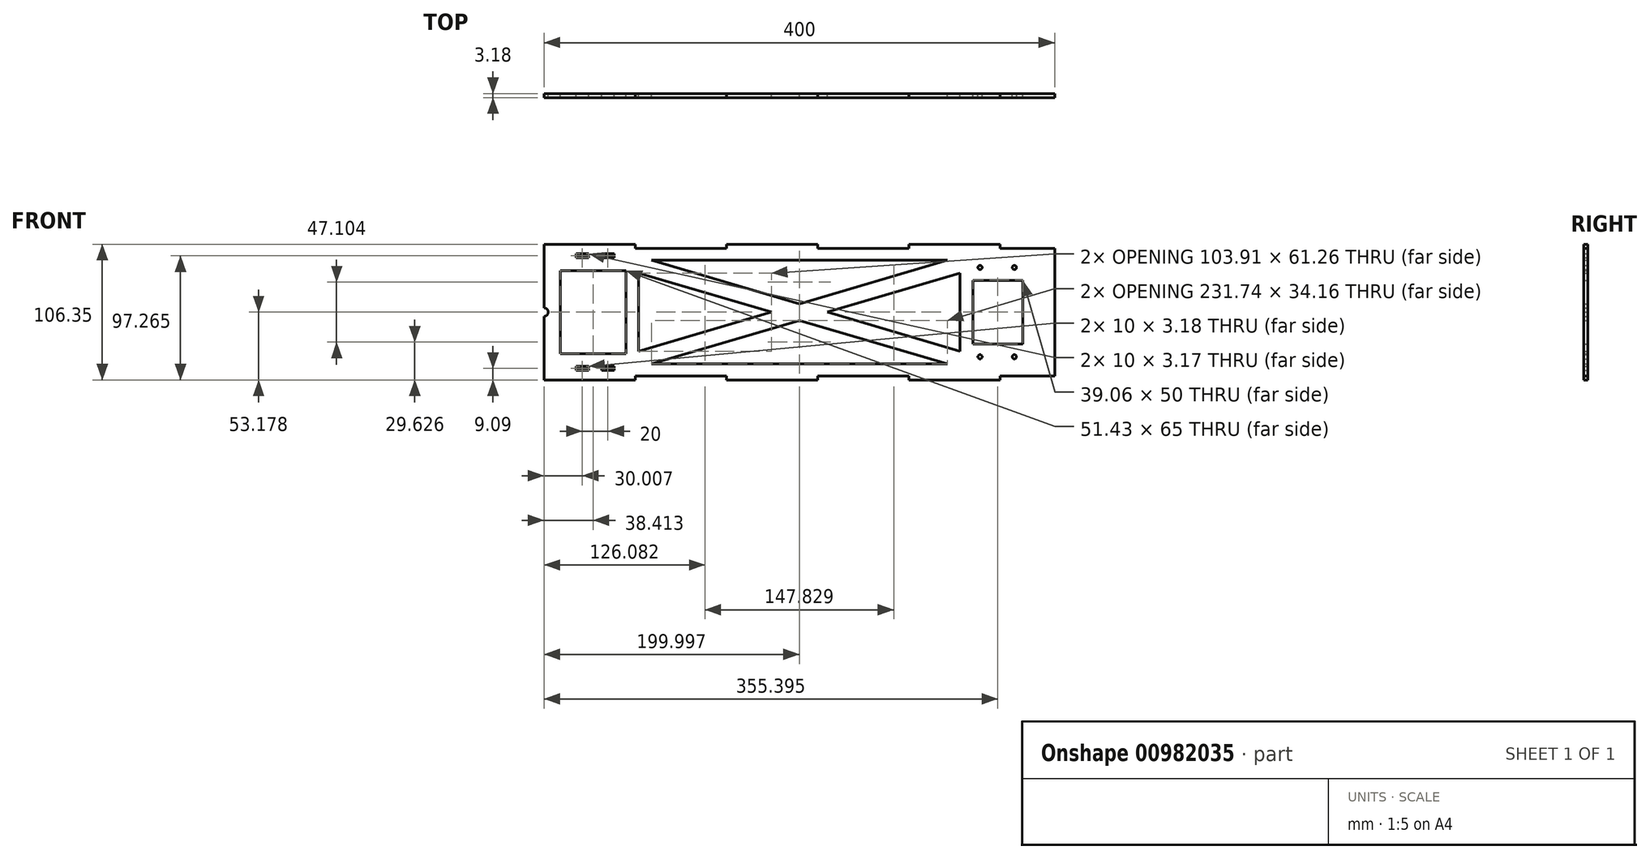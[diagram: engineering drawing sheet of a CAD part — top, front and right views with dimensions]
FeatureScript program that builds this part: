
annotation { "Feature Type Name" : "Feature", "Feature Type Description" : "" }
export const myFeature = defineFeature(function(context is Context, id is Id, definition is map)
    precondition{}
    {
        {
            var Q0;
            Q0=qCreatedBy(makeId("Front.planeOp"),FACE);
            var sketch = newSketch(context, id + "F0", { "sketchPlane" : qUnion([Q0])});
            skLineSegment(sketch, "E0.bottom", {"start": v(122.16, -35.2) * mm, "end": v(-277.84, -35.2) * mm, "construction": true});
            skLineSegment(sketch, "E0.top", {"start": v(122.16, 64.8) * mm, "end": v(-277.84, 64.8) * mm, "construction": true});
            skLineSegment(sketch, "E0.left", {"start": v(122.16, -35.2) * mm, "end": v(122.16, 64.8) * mm});
            skLineSegment(sketch, "E0.right", {"start": v(-277.84, -35.2) * mm, "end": v(-277.84, 64.8) * mm});
            skLineSegment(sketch, "E1", {"start": v(-237.84, 42.25) * mm, "end": v(-233.84, 42.25) * mm, "construction": true});
            skLineSegment(sketch, "E2", {"start": v(-237.84, 42.25) * mm, "end": v(-237.84, 46.25) * mm, "construction": true});
            skLineSegment(sketch, "E3", {"start": v(-237.84, -12.65) * mm, "end": v(-233.84, -12.65) * mm, "construction": true});
            skLineSegment(sketch, "E4", {"start": v(-237.84, -12.65) * mm, "end": v(-237.84, -8.65) * mm, "construction": true});
            skCircle(sketch, "E5", {"center": v(77.16, -20.2) * mm, "radius": 4 * mm, "construction": true});
            skLineSegment(sketch, "E6", {"start": v(77.16, -20.2) * mm, "end": v(81.16, -20.2) * mm, "construction": true});
            skLineSegment(sketch, "E7", {"start": v(77.16, -20.2) * mm, "end": v(77.16, -16.2) * mm, "construction": true});
            skCircle(sketch, "E8", {"center": v(90.63, -20.2) * mm, "radius": 1.64 * mm});
            skCircle(sketch, "E9.MirrorC", {"center": v(63.68, -20.2) * mm, "radius": 1.64 * mm});
            skCircle(sketch, "E10", {"center": v(77.16, 49.8) * mm, "radius": 4 * mm, "construction": true});
            skLineSegment(sketch, "E11", {"start": v(77.16, 49.8) * mm, "end": v(81.16, 49.8) * mm, "construction": true});
            skLineSegment(sketch, "E12", {"start": v(77.16, 49.8) * mm, "end": v(77.16, 53.8) * mm, "construction": true});
            skCircle(sketch, "E13", {"center": v(90.63, 49.8) * mm, "radius": 1.64 * mm});
            skCircle(sketch, "E14.MirrorC", {"center": v(63.68, 49.8) * mm, "radius": 1.64 * mm});
            skPoint(sketch, "E15.middle.positionSnap0", {"position": v(-237.84, -10.65) * mm});
            skPoint(sketch, "E15.centerSnap0", {"position": v(-237.84, -10.65) * mm});
            skLineSegment(sketch, "E16", {"start": v(-77.84, 64.8) * mm, "end": v(-77.84, -35.2) * mm, "construction": true});
            skLineSegment(sketch, "E17", {"start": v(-77.84, 14.8) * mm, "end": v(-277.84, 14.8) * mm, "construction": true});
            skLineSegment(sketch, "E18.right", {"start": v(-265.14, -17.7) * mm, "end": v(-265.14, 47.3) * mm});
            skLineSegment(sketch, "E19", {"start": v(-77.84, 14.8) * mm, "end": v(122.16, 14.8) * mm, "construction": true});
            skLineSegment(sketch, "E20.right", {"start": v(97.09, 39.8) * mm, "end": v(97.09, -10.2) * mm});
            skLineSegment(sketch, "E21.right", {"start": v(-213.71, 47.3) * mm, "end": v(-213.71, -17.7) * mm});
            skLineSegment(sketch, "E22", {"start": v(-265.14, 47.3) * mm, "end": v(-213.71, 47.3) * mm});
            skLineSegment(sketch, "E23", {"start": v(-265.14, -17.7) * mm, "end": v(-213.71, -17.7) * mm});
            skLineSegment(sketch, "E24.right", {"start": v(58.02, 39.8) * mm, "end": v(58.02, -10.2) * mm});
            skLineSegment(sketch, "E25", {"start": v(58.02, 39.8) * mm, "end": v(97.09, 39.8) * mm});
            skLineSegment(sketch, "E26", {"start": v(58.02, -10.2) * mm, "end": v(97.09, -10.2) * mm});
            skLineSegment(sketch, "E27.top", {"start": v(-277.84, -38.38) * mm, "end": v(-206.41, -38.38) * mm});
            skLineSegment(sketch, "E27.left", {"start": v(-277.84, -35.2) * mm, "end": v(-277.84, -38.38) * mm});
            skLineSegment(sketch, "E27.right", {"start": v(-206.41, -35.2) * mm, "end": v(-206.41, -38.38) * mm});
            skLineSegment(sketch, "E28.bottom", {"start": v(-206.41, -35.2) * mm, "end": v(-134.99, -35.2) * mm});
            skLineSegment(sketch, "E29.1.0.0", {"start": v(-134.99, -38.38) * mm, "end": v(-63.56, -38.38) * mm});
            skLineSegment(sketch, "E29.1.0.1", {"start": v(-63.56, -35.2) * mm, "end": v(7.87, -35.2) * mm});
            skLineSegment(sketch, "E29.1.0.2", {"start": v(-134.99, -35.2) * mm, "end": v(-134.99, -38.38) * mm});
            skLineSegment(sketch, "E29.1.0.3", {"start": v(-63.56, -35.2) * mm, "end": v(-63.56, -38.38) * mm});
            skLineSegment(sketch, "E29.1.0.4", {"start": v(-63.56, -35.2) * mm, "end": v(-63.56, -38.38) * mm});
            skLineSegment(sketch, "E29.2.0.0", {"start": v(7.87, -38.38) * mm, "end": v(79.3, -38.38) * mm});
            skLineSegment(sketch, "E29.2.0.2", {"start": v(7.87, -35.2) * mm, "end": v(7.87, -38.38) * mm});
            skLineSegment(sketch, "E29.direction1", {"start": v(-277.84, -38.38) * mm, "end": v(-134.99, -38.38) * mm, "construction": true});
            skLineSegment(sketch, "E30.MirrorCS", {"start": v(-63.56, 64.8) * mm, "end": v(-63.56, 67.97) * mm});
            skLineSegment(sketch, "E31.MirrorCS", {"start": v(-206.41, 64.8) * mm, "end": v(-206.41, 67.97) * mm});
            skLineSegment(sketch, "E32.MirrorCS", {"start": v(-134.99, 64.8) * mm, "end": v(-134.99, 67.97) * mm});
            skLineSegment(sketch, "E33.MirrorCS", {"start": v(-277.84, 64.8) * mm, "end": v(-277.84, 67.97) * mm});
            skLineSegment(sketch, "E34.MirrorCS", {"start": v(7.87, 64.8) * mm, "end": v(7.87, 67.97) * mm});
            skLineSegment(sketch, "E35.MirrorCS", {"start": v(-63.56, 64.8) * mm, "end": v(7.87, 64.8) * mm});
            skLineSegment(sketch, "E36.MirrorCS", {"start": v(-277.84, 67.97) * mm, "end": v(-206.41, 67.97) * mm});
            skLineSegment(sketch, "E37.MirrorCS", {"start": v(-206.41, 64.8) * mm, "end": v(-134.99, 64.8) * mm});
            skLineSegment(sketch, "E38.MirrorCS", {"start": v(7.87, 67.97) * mm, "end": v(79.3, 67.97) * mm});
            skLineSegment(sketch, "E39.MirrorCS", {"start": v(-277.84, 67.97) * mm, "end": v(-134.99, 67.97) * mm, "construction": true});
            skLineSegment(sketch, "E40.MirrorCS", {"start": v(-134.99, 67.97) * mm, "end": v(-63.56, 67.97) * mm});
            skLineSegment(sketch, "E41.MirrorCS", {"start": v(-222.83, -27.7) * mm, "end": v(-226, -27.7) * mm});
            skCircle(sketch, "E42.MirrorC", {"center": v(-237.83, -12.65) * mm, "radius": 2.35 * mm, "construction": true});
            skLineSegment(sketch, "E43.bottom", {"start": v(-252.83, -27.7) * mm, "end": v(-242.83, -27.7) * mm});
            skLineSegment(sketch, "E43.top", {"start": v(-252.83, -30.88) * mm, "end": v(-242.83, -30.88) * mm});
            skLineSegment(sketch, "E43.left", {"start": v(-252.83, -27.7) * mm, "end": v(-252.83, -30.88) * mm});
            skLineSegment(sketch, "E43.right", {"start": v(-242.83, -27.7) * mm, "end": v(-242.83, -30.88) * mm});
            skLineSegment(sketch, "E44.bottom", {"start": v(-222.83, -27.7) * mm, "end": v(-232.83, -27.7) * mm});
            skLineSegment(sketch, "E44.top", {"start": v(-222.83, -30.88) * mm, "end": v(-232.83, -30.88) * mm});
            skLineSegment(sketch, "E44.left", {"start": v(-222.83, -27.7) * mm, "end": v(-222.83, -30.88) * mm});
            skLineSegment(sketch, "E44.right", {"start": v(-232.83, -27.7) * mm, "end": v(-232.83, -30.88) * mm});
            skLineSegment(sketch, "E45.MirrorCS", {"start": v(-252.83, 57.3) * mm, "end": v(-252.83, 60.47) * mm});
            skLineSegment(sketch, "E46.MirrorCS", {"start": v(-222.83, 57.3) * mm, "end": v(-222.83, 60.47) * mm});
            skLineSegment(sketch, "E47.MirrorCS", {"start": v(-252.83, 60.47) * mm, "end": v(-242.83, 60.47) * mm});
            skLineSegment(sketch, "E48.MirrorCS", {"start": v(-222.83, 57.3) * mm, "end": v(-232.83, 57.3) * mm});
            skLineSegment(sketch, "E49.MirrorCS", {"start": v(-222.83, 60.47) * mm, "end": v(-232.83, 60.47) * mm});
            skCircle(sketch, "E50.MirrorC", {"center": v(-237.83, 42.25) * mm, "radius": 2.35 * mm, "construction": true});
            skLineSegment(sketch, "E51.MirrorCS", {"start": v(-252.83, 57.3) * mm, "end": v(-242.83, 57.3) * mm});
            skLineSegment(sketch, "E52.MirrorCS", {"start": v(-232.83, 57.3) * mm, "end": v(-232.83, 60.47) * mm});
            skLineSegment(sketch, "E53.MirrorCS", {"start": v(-242.83, 57.3) * mm, "end": v(-242.83, 60.47) * mm});
            skLineSegment(sketch, "E54", {"start": v(79.3, 67.97) * mm, "end": v(79.3, 64.8) * mm});
            skLineSegment(sketch, "E55", {"start": v(79.3, 64.8) * mm, "end": v(122.16, 64.8) * mm});
            skLineSegment(sketch, "E56", {"start": v(79.3, -38.38) * mm, "end": v(79.3, -35.2) * mm});
            skLineSegment(sketch, "E57", {"start": v(79.3, -35.2) * mm, "end": v(122.16, -35.2) * mm});
            skCircle(sketch, "E58", {"center": v(-277.84, 14.8) * mm, "radius": 3.3 * mm});
            skLineSegment(sketch, "E59.bottom", {"start": v(48.02, -25.83) * mm, "end": v(-203.71, -25.83) * mm});
            skLineSegment(sketch, "E59.top", {"start": v(48.02, 55.43) * mm, "end": v(-203.71, 55.43) * mm});
            skLineSegment(sketch, "E59.left", {"start": v(48.02, -25.83) * mm, "end": v(48.02, 55.43) * mm});
            skLineSegment(sketch, "E59.right", {"start": v(-203.71, -25.83) * mm, "end": v(-203.71, 55.43) * mm});
            skPoint(sketch, "E59.middle", {"position": v(-77.84, 14.8) * mm});
            skLineSegment(sketch, "E60", {"start": v(-203.71, 45.43) * mm, "end": v(38.02, -25.83) * mm});
            skLineSegment(sketch, "E61", {"start": v(-193.71, 55.43) * mm, "end": v(48.02, -15.83) * mm});
            skLineSegment(sketch, "E62.MirrorCS", {"start": v(38.02, 55.43) * mm, "end": v(-203.71, -15.83) * mm});
            skLineSegment(sketch, "E63.MirrorCS", {"start": v(48.02, 45.43) * mm, "end": v(-193.71, -25.83) * mm});
            skSolve(sketch);
        }
        {
            var Q0;
            Q0=makeQuery(id+"F0.imprint","IMPRINT",FACE,{"disambiguationData":[TD([[makeQuery(id+"F0.imprint","IMPRINT",EDGE,{"derivedFrom":sQuery(id+"F0.wireOp",EDGE,"E0.left")}),1.0]])]});
            var Q1;
            {var subQ1=sQuery(id+"F0.wireOp",EDGE,"MHkpmrzQ-DzUS-QcDW-mqt7-D2D0C6xKMiL6.top");var subQ6=sQuery(id+"F0.wireOp",EDGE,"MHkpmrzQ-DzUS-QcDW-mqt7-D2D0C6xKMiL6.right");var subQ10=makeQuery(id+"F0.imprint","INTERSECT",VERTEX,{"derivedFrom":[subQ1,subQ6]});Q1=makeQuery(id+"F0.imprint","IMPRINT",FACE,{"disambiguationData":[TD([[makeQuery(id+"F0.imprint","IMPRINT",EDGE,{"disambiguationData":[TD([[subQ10,1.0]])],"derivedFrom":subQ1}),1.0]])]});}
            var Q2;
            {var subQ6=sQuery(id+"F0.wireOp",EDGE,"MHkpmrzQ-DzUS-QcDW-mqt7-D2D0C6xKMiL6.top");var subQ9=sQuery(id+"F0.wireOp",EDGE,"MHkpmrzQ-DzUS-QcDW-mqt7-D2D0C6xKMiL6.left");var subQ10=makeQuery(id+"F0.imprint","INTERSECT",VERTEX,{"derivedFrom":[subQ6,subQ9]});Q2=makeQuery(id+"F0.imprint","IMPRINT",FACE,{"disambiguationData":[TD([[makeQuery(id+"F0.imprint","IMPRINT",EDGE,{"disambiguationData":[TD([[subQ10,-1.0]])],"derivedFrom":subQ6}),1.0]])]});}
            var Q3;
            {var subQ0=sQuery(id+"F0.wireOp",EDGE,"7W97gwla-n0WM-y60X-97Ln-5MnTus8xXd5n");var subQ1=sQuery(id+"F0.wireOp",EDGE,"MHkpmrzQ-DzUS-QcDW-mqt7-D2D0C6xKMiL6.bottom");var subQ2=makeQuery(id+"F0.imprint","INTERSECT",VERTEX,{"derivedFrom":[subQ1,subQ0]});Q3=makeQuery(id+"F0.imprint","IMPRINT",FACE,{"disambiguationData":[TD([[makeQuery(id+"F0.imprint","IMPRINT",EDGE,{"disambiguationData":[TD([[subQ2,1.0]])],"derivedFrom":subQ1}),-1.0]])]});}
            var Q4;
            {var subQ1=sQuery(id+"F0.wireOp",EDGE,"MHkpmrzQ-DzUS-QcDW-mqt7-D2D0C6xKMiL6.right");var subQ7=sQuery(id+"F0.wireOp",EDGE,"MHkpmrzQ-DzUS-QcDW-mqt7-D2D0C6xKMiL6.bottom");var subQ8=makeQuery(id+"F0.imprint","INTERSECT",VERTEX,{"derivedFrom":[subQ7,subQ1]});Q4=makeQuery(id+"F0.imprint","IMPRINT",FACE,{"disambiguationData":[TD([[makeQuery(id+"F0.imprint","IMPRINT",EDGE,{"disambiguationData":[TD([[subQ8,1.0]])],"derivedFrom":subQ7}),-1.0]])]});}
            var Q5;
            {var subQ1=sQuery(id+"F0.wireOp",EDGE,"MHkpmrzQ-DzUS-QcDW-mqt7-D2D0C6xKMiL6.bottom");var subQ7=sQuery(id+"F0.wireOp",EDGE,"wyMJddfo-exag-QAAZ-zDEC-KmLDTo5ackwH.right");var subQ9=makeQuery(id+"F0.imprint","INTERSECT",VERTEX,{"derivedFrom":[subQ1,subQ7]});Q5=makeQuery(id+"F0.imprint","IMPRINT",FACE,{"disambiguationData":[TD([[makeQuery(id+"F0.imprint","IMPRINT",EDGE,{"disambiguationData":[TD([[subQ9,1.0]])],"derivedFrom":subQ1}),-1.0]])]});}
            var Q6;
            {var subQ0=sQuery(id+"F0.wireOp",EDGE,"wyMJddfo-exag-QAAZ-zDEC-KmLDTo5ackwH.left");var subQ1=sQuery(id+"F0.wireOp",EDGE,"7W97gwla-n0WM-y60X-97Ln-5MnTus8xXd5n");var subQ2=makeQuery(id+"F0.imprint","INTERSECT",VERTEX,{"derivedFrom":[subQ1,subQ0]});Q6=makeQuery(id+"F0.imprint","IMPRINT",FACE,{"disambiguationData":[TD([[makeQuery(id+"F0.imprint","IMPRINT",EDGE,{"disambiguationData":[TD([[subQ2,1.0]])],"derivedFrom":subQ1}),1.0]])]});}
            var Q7;
            {var subQ0=sQuery(id+"F0.wireOp",EDGE,"wyMJddfo-exag-QAAZ-zDEC-KmLDTo5ackwH.right");var subQ1=sQuery(id+"F0.wireOp",EDGE,"7W97gwla-n0WM-y60X-97Ln-5MnTus8xXd5n");var subQ2=makeQuery(id+"F0.imprint","INTERSECT",VERTEX,{"derivedFrom":[subQ1,subQ0]});Q7=makeQuery(id+"F0.imprint","IMPRINT",FACE,{"disambiguationData":[TD([[makeQuery(id+"F0.imprint","IMPRINT",EDGE,{"disambiguationData":[TD([[subQ2,-1.0]])],"derivedFrom":subQ1}),-1.0]])]});}
            var Q8;
            {var subQ0=sQuery(id+"F0.wireOp",EDGE,"wyMJddfo-exag-QAAZ-zDEC-KmLDTo5ackwH.right");var subQ1=sQuery(id+"F0.wireOp",EDGE,"7W97gwla-n0WM-y60X-97Ln-5MnTus8xXd5n");var subQ2=makeQuery(id+"F0.imprint","INTERSECT",VERTEX,{"derivedFrom":[subQ1,subQ0]});Q8=makeQuery(id+"F0.imprint","IMPRINT",FACE,{"disambiguationData":[TD([[makeQuery(id+"F0.imprint","IMPRINT",EDGE,{"disambiguationData":[TD([[subQ2,1.0]])],"derivedFrom":subQ1}),1.0]])]});}
            var Q9;
            {var subQ3=sQuery(id+"F0.wireOp",EDGE,"7W97gwla-n0WM-y60X-97Ln-5MnTus8xXd5n");var subQ9=sQuery(id+"F0.wireOp",EDGE,"wyMJddfo-exag-QAAZ-zDEC-KmLDTo5ackwH.right");var subQ10=makeQuery(id+"F0.imprint","INTERSECT",VERTEX,{"derivedFrom":[subQ3,subQ9]});Q9=makeQuery(id+"F0.imprint","IMPRINT",FACE,{"disambiguationData":[TD([[makeQuery(id+"F0.imprint","IMPRINT",EDGE,{"disambiguationData":[TD([[subQ10,-1.0]])],"derivedFrom":subQ3}),1.0]])]});}
            var Q10;
            {var subQ0=sQuery(id+"F0.wireOp",EDGE,"wyMJddfo-exag-QAAZ-zDEC-KmLDTo5ackwH.left");var subQ1=sQuery(id+"F0.wireOp",EDGE,"NQHkE6QF-ssxk-nDWH-MouS-YJdmpnpYr1Nf");var subQ2=makeQuery(id+"F0.imprint","INTERSECT",VERTEX,{"derivedFrom":[subQ1,subQ0]});Q10=makeQuery(id+"F0.imprint","IMPRINT",FACE,{"disambiguationData":[TD([[makeQuery(id+"F0.imprint","IMPRINT",EDGE,{"disambiguationData":[TD([[subQ2,1.0]])],"derivedFrom":subQ1}),1.0]])]});}
            var Q11;
            {var subQ0=sQuery(id+"F0.wireOp",EDGE,"wyMJddfo-exag-QAAZ-zDEC-KmLDTo5ackwH.right");var subQ1=sQuery(id+"F0.wireOp",EDGE,"NQHkE6QF-ssxk-nDWH-MouS-YJdmpnpYr1Nf");var subQ2=makeQuery(id+"F0.imprint","INTERSECT",VERTEX,{"derivedFrom":[subQ1,subQ0]});Q11=makeQuery(id+"F0.imprint","IMPRINT",FACE,{"disambiguationData":[TD([[makeQuery(id+"F0.imprint","IMPRINT",EDGE,{"disambiguationData":[TD([[subQ2,-1.0]])],"derivedFrom":subQ1}),-1.0]])]});}
            var Q12;
            {var subQ5=sQuery(id+"F0.wireOp",EDGE,"wyMJddfo-exag-QAAZ-zDEC-KmLDTo5ackwH.right");var subQ7=sQuery(id+"F0.wireOp",EDGE,"MHkpmrzQ-DzUS-QcDW-mqt7-D2D0C6xKMiL6.top");var subQ9=makeQuery(id+"F0.imprint","INTERSECT",VERTEX,{"derivedFrom":[subQ7,subQ5]});Q12=makeQuery(id+"F0.imprint","IMPRINT",FACE,{"disambiguationData":[TD([[makeQuery(id+"F0.imprint","IMPRINT",EDGE,{"disambiguationData":[TD([[subQ9,1.0]])],"derivedFrom":subQ7}),1.0]])]});}
            var Q13;
            {var subQ0=sQuery(id+"F0.wireOp",EDGE,"ec5e1f7f-dad6-47e2-b572-f540bd572ffd0.MirrorCS");var subQ1=sQuery(id+"F0.wireOp",EDGE,"NQHkE6QF-ssxk-nDWH-MouS-YJdmpnpYr1Nf");var subQ2=makeQuery(id+"F0.imprint","INTERSECT",VERTEX,{"derivedFrom":[subQ1,subQ0]});Q13=makeQuery(id+"F0.imprint","IMPRINT",FACE,{"disambiguationData":[TD([[makeQuery(id+"F0.imprint","IMPRINT",EDGE,{"disambiguationData":[TD([[subQ2,1.0]])],"derivedFrom":subQ1}),-1.0]])]});}
            var Q14;
            {var subQ3=sQuery(id+"F0.wireOp",EDGE,"E59.right");var subQ5=sQuery(id+"F0.wireOp",EDGE,"E59.top");var subQ6=makeQuery(id+"F0.imprint","INTERSECT",VERTEX,{"derivedFrom":[subQ5,subQ3]});Q14=makeQuery(id+"F0.imprint","IMPRINT",FACE,{"disambiguationData":[TD([[makeQuery(id+"F0.imprint","IMPRINT",EDGE,{"disambiguationData":[TD([[subQ6,1.0]])],"derivedFrom":subQ5}),1.0]])]});}
            var Q15;
            {var subQ1=sQuery(id+"F0.wireOp",EDGE,"E59.right");var subQ7=sQuery(id+"F0.wireOp",EDGE,"E59.bottom");var subQ8=makeQuery(id+"F0.imprint","INTERSECT",VERTEX,{"derivedFrom":[subQ7,subQ1]});Q15=makeQuery(id+"F0.imprint","IMPRINT",FACE,{"disambiguationData":[TD([[makeQuery(id+"F0.imprint","IMPRINT",EDGE,{"disambiguationData":[TD([[subQ8,1.0]])],"derivedFrom":subQ7}),-1.0]])]});}
            var Q16;
            {var subQ0=sQuery(id+"F0.wireOp",EDGE,"E60");var subQ1=sQuery(id+"F0.wireOp",EDGE,"E59.bottom");var subQ2=makeQuery(id+"F0.imprint","INTERSECT",VERTEX,{"derivedFrom":[subQ1,subQ0]});Q16=makeQuery(id+"F0.imprint","IMPRINT",FACE,{"disambiguationData":[TD([[makeQuery(id+"F0.imprint","IMPRINT",EDGE,{"disambiguationData":[TD([[subQ2,1.0]])],"derivedFrom":subQ1}),-1.0]])]});}
            var Q17;
            {var subQ3=sQuery(id+"F0.wireOp",EDGE,"E62.MirrorCS");var subQ5=sQuery(id+"F0.wireOp",EDGE,"E59.top");var subQ6=makeQuery(id+"F0.imprint","INTERSECT",VERTEX,{"derivedFrom":[subQ5,subQ3]});Q17=makeQuery(id+"F0.imprint","IMPRINT",FACE,{"disambiguationData":[TD([[makeQuery(id+"F0.imprint","IMPRINT",EDGE,{"disambiguationData":[TD([[subQ6,1.0]])],"derivedFrom":subQ5}),1.0]])]});}
            var Q18;
            {var subQ0=sQuery(id+"F0.wireOp",EDGE,"E63.MirrorCS");var subQ1=sQuery(id+"F0.wireOp",EDGE,"E60");var subQ2=makeQuery(id+"F0.imprint","INTERSECT",VERTEX,{"derivedFrom":[subQ1,subQ0]});Q18=makeQuery(id+"F0.imprint","IMPRINT",FACE,{"disambiguationData":[TD([[makeQuery(id+"F0.imprint","IMPRINT",EDGE,{"disambiguationData":[TD([[subQ2,1.0]])],"derivedFrom":subQ1}),1.0]])]});}
            extrude(context, id + "F1", {"entities" : qUnion([Q0, Q1, Q2, Q3, Q4, Q5, Q6, Q7, Q8, Q9, Q10, Q11, Q12, Q13, Q14, Q15, Q16, Q17, Q18]), "depth" : 3.17 * mm, "offsetDistance" : 25.4 * mm});
        }
    });
